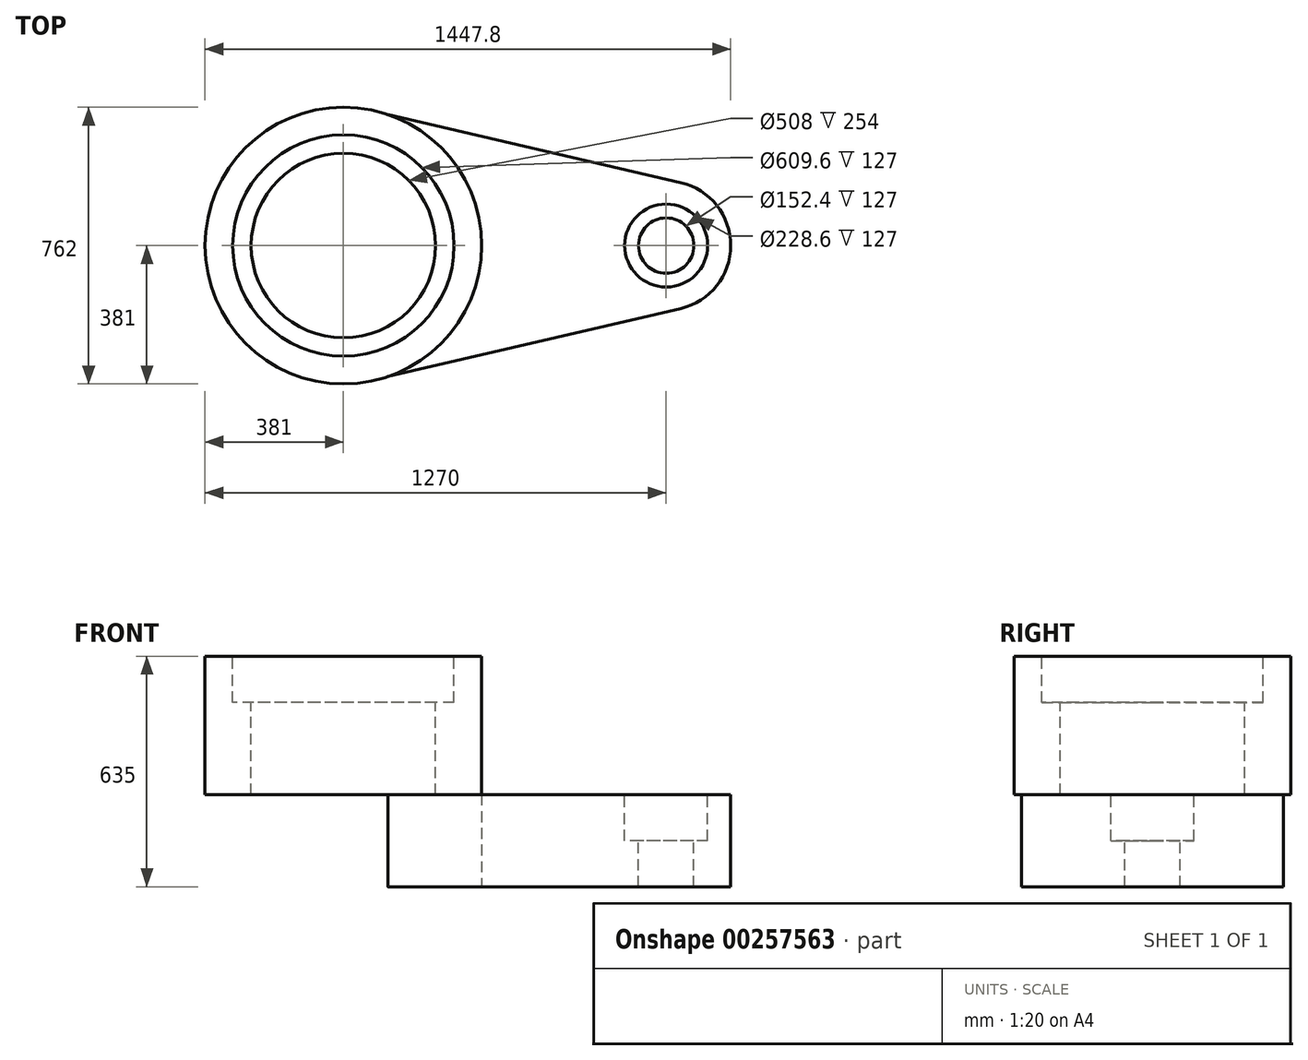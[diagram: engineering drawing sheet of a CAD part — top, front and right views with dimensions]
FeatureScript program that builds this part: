
annotation { "Feature Type Name" : "Feature", "Feature Type Description" : "" }
export const myFeature = defineFeature(function(context is Context, id is Id, definition is map)
    precondition{}
    {
        {
            var Q0;
            Q0=qCreatedBy(makeId("Top.planeOp"),FACE);
            var sketch = newSketch(context, id + "F0", { "sketchPlane" : qUnion([Q0])});
            skCircle(sketch, "E0", {"center": v(0, 0) * mm, "radius": 381 * mm});
            skArc(sketch, "E1", {"start": v(929.26, -173.18) * mm, "mid": v(1066.8, 0) * mm, "end": v(929.27, 173.18) * mm});
            skLineSegment(sketch, "E2", {"start": v(49.42, 377.78) * mm, "end": v(929.27, 173.18) * mm});
            skLineSegment(sketch, "E3", {"start": v(48.89, -377.85) * mm, "end": v(929.26, -173.18) * mm});
            skLineSegment(sketch, "E4.MirrorCS", {"start": v(-49.42, 377.78) * mm, "end": v(-929.27, 173.18) * mm});
            skArc(sketch, "E5.MirrorCS", {"start": v(-929.26, -173.18) * mm, "mid": v(-1066.8, 0) * mm, "end": v(-929.27, 173.18) * mm});
            skLineSegment(sketch, "E6.MirrorCS", {"start": v(-48.89, -377.85) * mm, "end": v(-929.26, -173.18) * mm});
            skSolve(sketch);
        }
        {
            var Q0;
            {var subQ0=sQuery(id+"F0.wireOp",EDGE,"E5.MirrorCS");Q0=makeQuery(id+"F0.imprint","IMPRINT",FACE,{"disambiguationData":[TD([[makeQuery(id+"F0.imprint","IMPRINT",EDGE,{"derivedFrom":subQ0}),-1.0]])]});}
            var Q1;
            {var subQ0=sQuery(id+"F0.wireOp",EDGE,"E0");var subQ1=sQuery(id+"F0.wireOp",EDGE,"E2");var subQ2=makeQuery(id+"F0.imprint","INTERSECT",VERTEX,{"disambiguationData":[OD(0.0)],"derivedFrom":[subQ1,subQ0]});Q1=makeQuery(id+"F0.imprint","IMPRINT",FACE,{"disambiguationData":[TD([[makeQuery(id+"F0.imprint","IMPRINT",EDGE,{"disambiguationData":[TD([[subQ2,-1.0]])],"derivedFrom":subQ1}),-1.0]])]});}
            var Q2;
            {var subQ0=sQuery(id+"F0.wireOp",EDGE,"E1");Q2=makeQuery(id+"F0.imprint","IMPRINT",FACE,{"disambiguationData":[TD([[makeQuery(id+"F0.imprint","IMPRINT",EDGE,{"derivedFrom":subQ0}),1.0]])]});}
            extrude(context, id + "F1", {"entities" : qUnion([Q0, Q1, Q2]), "depth" : 254 * mm});
        }
        {
            var Q0;
            Q0=makeQuery(id+"F1.opExtrude","CAP_FACE",FACE,{"disambiguationData":[OSD([sQuery(id+"F0.wireOp",EDGE,"E1"),sQuery(id+"F0.wireOp",EDGE,"E2"),sQuery(id+"F0.wireOp",EDGE,"E3"),sQuery(id+"F0.wireOp",EDGE,"E4.MirrorCS"),sQuery(id+"F0.wireOp",EDGE,"E0"),sQuery(id+"F0.wireOp",EDGE,"E5.MirrorCS"),sQuery(id+"F0.wireOp",EDGE,"E6.MirrorCS")])],"isStart":false});
            var sketch = newSketch(context, id + "F2", { "sketchPlane" : qUnion([Q0])});
            skArc(sketch, "E7.0", {"start": v(49.42, 377.78) * mm, "mid": v(0, 381) * mm, "end": v(-49.42, 377.78) * mm});
            skArc(sketch, "E8.0.1", {"start": v(-48.89, -377.85) * mm, "mid": v(0, -381) * mm, "end": v(48.89, -377.85) * mm});
            skCircle(sketch, "E9", {"center": v(0, 0) * mm, "radius": 381 * mm});
            skSolve(sketch);
        }
        {
            var Q0;
            Q0 = qSketchRegion(id + "F2", true);
            extrude(context, id + "F3", {"entities" : qUnion([Q0]), "operationType" : NewBodyOperationType.ADD, "depth" : 381 * mm});
        }
        {
            var Q0;
            Q0=makeQuery(id+"F3.opExtrude","CAP_FACE",FACE,{"disambiguationData":[OSD([sQuery(id+"F2.wireOp",EDGE,"E9")])],"isStart":false});
            var sketch = newSketch(context, id + "F4", { "sketchPlane" : qUnion([Q0])});
            skCircle(sketch, "E10", {"center": v(0, 0) * mm, "radius": 254 * mm});
            skSolve(sketch);
        }
        {
            var Q0;
            Q0 = qSketchRegion(id + "F4", true);
            extrude(context, id + "F5", {"entities" : qUnion([Q0]), "operationType" : NewBodyOperationType.REMOVE, "oppositeDirection" : true, "depth" : 635 * mm});
        }
        {
            var Q0;
            Q0=makeQuery(id+"F3.opExtrude","CAP_FACE",FACE,{"disambiguationData":[OSD([sQuery(id+"F2.wireOp",EDGE,"E9")])],"isStart":false});
            var sketch = newSketch(context, id + "F6", { "sketchPlane" : qUnion([Q0])});
            skCircle(sketch, "E11", {"center": v(0, 0) * mm, "radius": 304.8 * mm});
            skSolve(sketch);
        }
        {
            var Q0;
            Q0 = qSketchRegion(id + "F6", true);
            extrude(context, id + "F7", {"entities" : qUnion([Q0]), "operationType" : NewBodyOperationType.REMOVE, "oppositeDirection" : true, "depth" : 127 * mm});
        }
        {
            var Q0;
            {var subQ0=sQuery(id+"F0.wireOp",EDGE,"E5.MirrorCS");var subQ1=sQuery(id+"F0.wireOp",EDGE,"E0");var subQ2=sQuery(id+"F0.wireOp",EDGE,"E3");var subQ3=sQuery(id+"F0.wireOp",EDGE,"E6.MirrorCS");var subQ4=sQuery(id+"F0.wireOp",EDGE,"E2");var subQ5=sQuery(id+"F0.wireOp",EDGE,"E4.MirrorCS");Q0=makeQuery(id+"F3.boolean.opBoolean","SPLIT",FACE,{"disambiguationData":[TD([makeQuery(id+"F1.opExtrude","SWEPT_FACE",FACE,{"disambiguationData":[OSD([subQ5])]})])],"derivedFrom":makeQuery(id+"F1.opExtrude","CAP_FACE",FACE,{"disambiguationData":[OSD([sQuery(id+"F0.wireOp",EDGE,"E1"),subQ4,subQ2,subQ5,subQ1,subQ0,subQ3])],"isStart":false})});}
            var sketch = newSketch(context, id + "F8", { "sketchPlane" : qUnion([Q0])});
            skLineSegment(sketch, "E12", {"start": v(-1094.24, 0) * mm, "end": v(1103.32, 0) * mm, "construction": true});
            skCircle(sketch, "E13", {"center": v(889, 0) * mm, "radius": 76.2 * mm});
            skCircle(sketch, "E14", {"center": v(-889, 0) * mm, "radius": 76.2 * mm});
            skSolve(sketch);
        }
        {
            var Q0;
            Q0 = qSketchRegion(id + "F8", true);
            extrude(context, id + "F9", {"entities" : qUnion([Q0]), "operationType" : NewBodyOperationType.REMOVE, "oppositeDirection" : true, "depth" : 254 * mm});
        }
        {
            var Q0;
            {var subQ0=sQuery(id+"F0.wireOp",EDGE,"E5.MirrorCS");var subQ1=sQuery(id+"F0.wireOp",EDGE,"E0");var subQ2=sQuery(id+"F0.wireOp",EDGE,"E3");var subQ3=sQuery(id+"F0.wireOp",EDGE,"E6.MirrorCS");var subQ4=sQuery(id+"F0.wireOp",EDGE,"E2");var subQ5=sQuery(id+"F0.wireOp",EDGE,"E4.MirrorCS");Q0=makeQuery(id+"F3.boolean.opBoolean","SPLIT",FACE,{"disambiguationData":[TD([makeQuery(id+"F1.opExtrude","SWEPT_FACE",FACE,{"disambiguationData":[OSD([subQ5])]})])],"derivedFrom":makeQuery(id+"F1.opExtrude","CAP_FACE",FACE,{"disambiguationData":[OSD([sQuery(id+"F0.wireOp",EDGE,"E1"),subQ4,subQ2,subQ5,subQ1,subQ0,subQ3])],"isStart":false})});}
            var sketch = newSketch(context, id + "F10", { "sketchPlane" : qUnion([Q0])});
            skCircle(sketch, "E15", {"center": v(-889, 0) * mm, "radius": 114.3 * mm});
            skSolve(sketch);
        }
        {
            var Q0;
            Q0 = qSketchRegion(id + "F10", true);
            extrude(context, id + "F11", {"entities" : qUnion([Q0]), "operationType" : NewBodyOperationType.REMOVE, "oppositeDirection" : true, "depth" : 127 * mm});
        }
        {
            var Q0;
            {var subQ0=sQuery(id+"F0.wireOp",EDGE,"E0");var subQ1=sQuery(id+"F0.wireOp",EDGE,"E2");var subQ2=sQuery(id+"F0.wireOp",EDGE,"E4.MirrorCS");var subQ3=sQuery(id+"F0.wireOp",EDGE,"E3");var subQ5=sQuery(id+"F0.wireOp",EDGE,"E1");var subQ6=sQuery(id+"F0.wireOp",EDGE,"E6.MirrorCS");Q0=makeQuery(id+"F3.boolean.opBoolean","SPLIT",FACE,{"disambiguationData":[TD([makeQuery(id+"F1.opExtrude","SWEPT_FACE",FACE,{"disambiguationData":[OSD([subQ5])]})])],"derivedFrom":makeQuery(id+"F1.opExtrude","CAP_FACE",FACE,{"disambiguationData":[OSD([subQ5,subQ1,subQ3,subQ2,subQ0,sQuery(id+"F0.wireOp",EDGE,"E5.MirrorCS"),subQ6])],"isStart":false})});}
            var sketch = newSketch(context, id + "F12", { "sketchPlane" : qUnion([Q0])});
            skCircle(sketch, "E16", {"center": v(889, 0) * mm, "radius": 114.3 * mm});
            skSolve(sketch);
        }
        {
            var Q0;
            Q0 = qSketchRegion(id + "F12", true);
            extrude(context, id + "F13", {"entities" : qUnion([Q0]), "operationType" : NewBodyOperationType.REMOVE, "oppositeDirection" : true, "depth" : 127 * mm});
        }
    });
